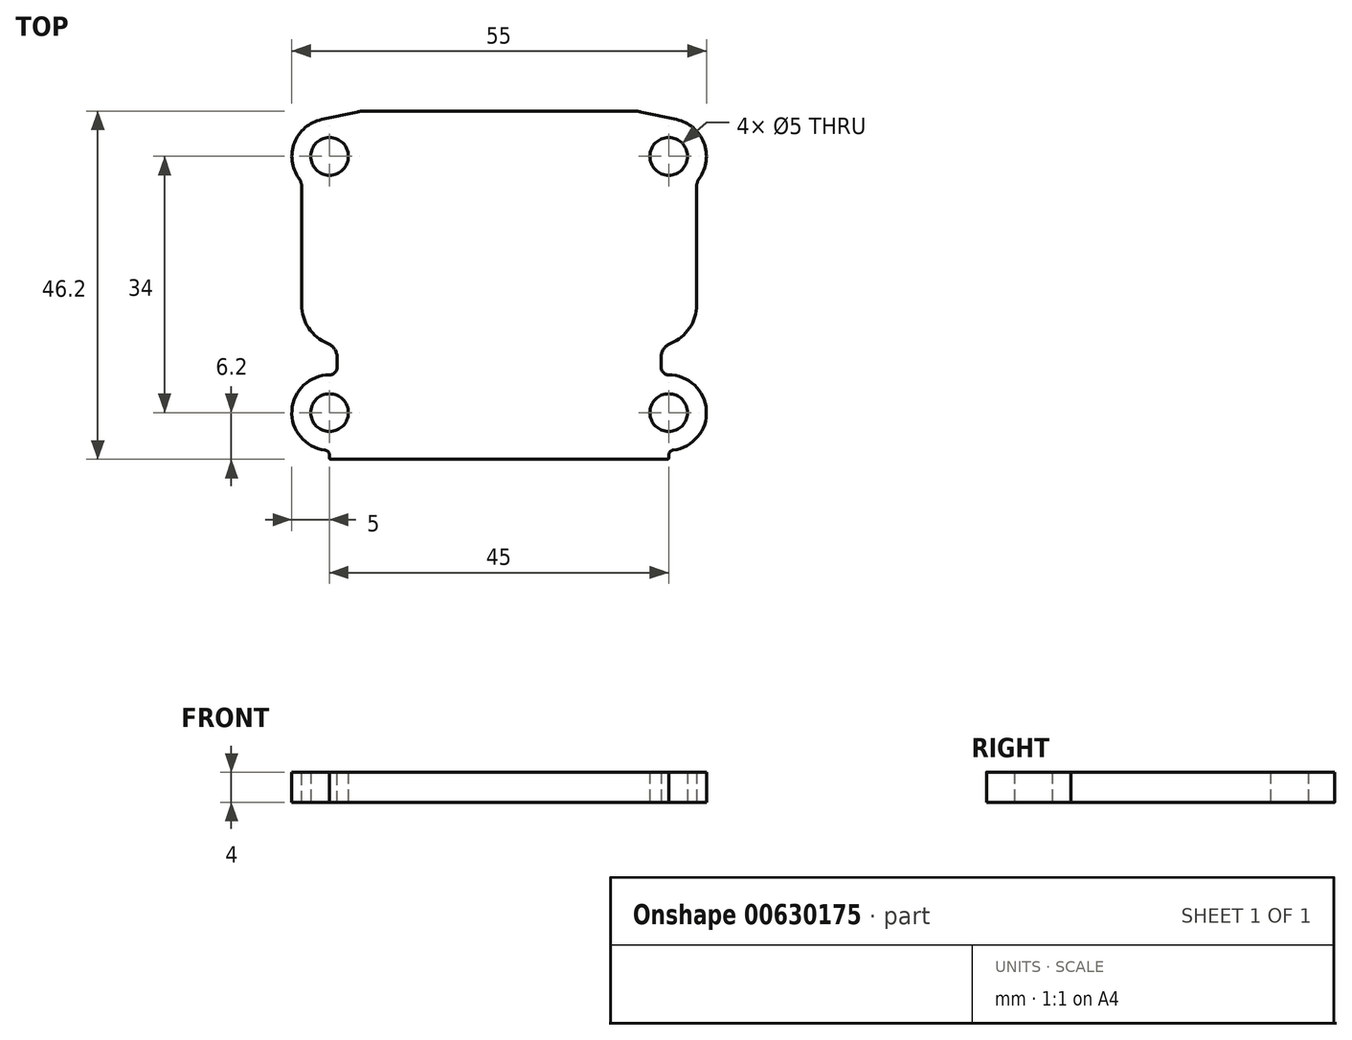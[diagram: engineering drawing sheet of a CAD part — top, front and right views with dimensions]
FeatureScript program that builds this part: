
annotation { "Feature Type Name" : "Feature", "Feature Type Description" : "" }
export const myFeature = defineFeature(function(context is Context, id is Id, definition is map)
    precondition{}
    {
        {
            var Q0;
            Q0=qCreatedBy(makeId("Top.planeOp"),FACE);
            var sketch = newSketch(context, id + "F0", { "sketchPlane" : qUnion([Q0])});
            skLineSegment(sketch, "E0.bottom", {"start": v(0, 0) * mm, "end": v(-45, 0) * mm, "construction": true});
            skLineSegment(sketch, "E0.top", {"start": v(0, 34) * mm, "end": v(-45, 34) * mm, "construction": true});
            skLineSegment(sketch, "E0.left", {"start": v(0, 0) * mm, "end": v(0, 34) * mm, "construction": true});
            skLineSegment(sketch, "E0.right", {"start": v(-45, 0) * mm, "end": v(-45, 34) * mm, "construction": true});
            skCircle(sketch, "E1", {"center": v(-45, 34) * mm, "radius": 2.5 * mm});
            skCircle(sketch, "E2", {"center": v(-45, 0) * mm, "radius": 2.5 * mm});
            skCircle(sketch, "E3", {"center": v(0, 0) * mm, "radius": 2.5 * mm});
            skArc(sketch, "E4", {"start": v(-44, 4.9) * mm, "mid": v(-49.97, 0.5) * mm, "end": v(-45, -5) * mm});
            skArc(sketch, "E5", {"start": v(0, -5) * mm, "mid": v(4.97, 0.5) * mm, "end": v(-1, 4.9) * mm});
            skLineSegment(sketch, "E6", {"start": v(-48.7, 30.64) * mm, "end": v(-48.7, 14.3) * mm});
            skLineSegment(sketch, "E7", {"start": v(-46.04, 38.9) * mm, "end": v(1.04, 38.9) * mm, "construction": true});
            skLineSegment(sketch, "E8", {"start": v(3.7, 30.64) * mm, "end": v(3.7, 14.3) * mm});
            skLineSegment(sketch, "E9", {"start": v(-40.82, 40) * mm, "end": v(-4.18, 40) * mm});
            skLineSegment(sketch, "E10", {"start": v(-4.18, 40) * mm, "end": v(1.04, 38.9) * mm});
            skLineSegment(sketch, "E11", {"start": v(-40.82, 40) * mm, "end": v(-46.04, 38.9) * mm});
            skLineSegment(sketch, "E12", {"start": v(-48.7, 14.3) * mm, "end": v(3.7, 14.3) * mm, "construction": true});
            skArc(sketch, "E13", {"start": v(-48.7, 14.3) * mm, "mid": v(-47.36, 10.7) * mm, "end": v(-44, 8.86) * mm});
            skArc(sketch, "E14", {"start": v(-1, 8.86) * mm, "mid": v(2.36, 10.7) * mm, "end": v(3.7, 14.3) * mm});
            skPoint(sketch, "E15", {"position": v(-45, 31.5) * mm});
            skPoint(sketch, "E16", {"position": v(-45, 2.5) * mm});
            skLineSegment(sketch, "E17.top", {"start": v(-45, -6.2) * mm, "end": v(0, -6.2) * mm});
            skLineSegment(sketch, "E17.left", {"start": v(-45, -5) * mm, "end": v(-45, -6.2) * mm});
            skLineSegment(sketch, "E17.right", {"start": v(0, -5) * mm, "end": v(0, -6.2) * mm});
            skLineSegment(sketch, "E18", {"start": v(-42.5, 0) * mm, "end": v(-42.5, 8.84) * mm, "construction": true});
            skLineSegment(sketch, "E19", {"start": v(-2.5, 0) * mm, "end": v(-2.5, 8.84) * mm, "construction": true});
            skLineSegment(sketch, "E20", {"start": v(-44, 8.86) * mm, "end": v(-44, 4.9) * mm});
            skLineSegment(sketch, "E21", {"start": v(-1, 8.86) * mm, "end": v(-1, 4.9) * mm});
            skCircle(sketch, "E22", {"center": v(0, 34) * mm, "radius": 2.5 * mm});
            skArc(sketch, "E23", {"start": v(-46.04, 38.9) * mm, "mid": v(-49.76, 35.53) * mm, "end": v(-48.7, 30.64) * mm});
            skArc(sketch, "E24", {"start": v(3.7, 30.64) * mm, "mid": v(4.76, 35.53) * mm, "end": v(1.04, 38.9) * mm});
            skSolve(sketch);
        }
        {
            var Q0;
            Q0 = qSketchRegion(id + "F0", true);
            extrude(context, id + "F1", {"entities" : qUnion([Q0]), "depth" : 4 * mm, "offsetDistance" : 25 * mm});
        }
        {
            var Q0;
            Q0=makeQuery(id+"F1.opExtrude","SWEPT_EDGE",EDGE,{"disambiguationData":[OSD([sQuery(id+"F0.wireOp",EDGE,"E13"),sQuery(id+"F0.wireOp",EDGE,"E20")])]});
            var Q1;
            Q1=makeQuery(id+"F1.opExtrude","SWEPT_EDGE",EDGE,{"disambiguationData":[OSD([sQuery(id+"F0.wireOp",EDGE,"E14"),sQuery(id+"F0.wireOp",EDGE,"E21")])]});
            fillet(context, id + "F2", {"entities" : qUnion([Q0, Q1]), "radius" : 2 * mm, "tangentPropagation" : true, "allowEdgeOverflow" : false});
        }
        {
            var Q0;
            Q0=makeQuery(id+"F1.opExtrude","SWEPT_EDGE",EDGE,{"disambiguationData":[OSD([sQuery(id+"F0.wireOp",EDGE,"E5"),sQuery(id+"F0.wireOp",EDGE,"E21")])]});
            var Q1;
            Q1=makeQuery(id+"F1.opExtrude","SWEPT_EDGE",EDGE,{"disambiguationData":[OSD([sQuery(id+"F0.wireOp",EDGE,"E4"),sQuery(id+"F0.wireOp",EDGE,"E20")])]});
            fillet(context, id + "F3", {"entities" : qUnion([Q0, Q1]), "radius" : 1 * mm, "tangentPropagation" : true, "allowEdgeOverflow" : false});
        }
        {
            var Q0;
            Q0=makeQuery(id+"F1.opExtrude","SWEPT_EDGE",EDGE,{"disambiguationData":[OSD([sQuery(id+"F0.wireOp",EDGE,"E4"),sQuery(id+"F0.wireOp",EDGE,"E17.left")])]});
            var Q1;
            Q1=makeQuery(id+"F1.opExtrude","SWEPT_EDGE",EDGE,{"disambiguationData":[OSD([sQuery(id+"F0.wireOp",EDGE,"E5"),sQuery(id+"F0.wireOp",EDGE,"E17.right")])]});
            fillet(context, id + "F4", {"entities" : qUnion([Q0, Q1]), "radius" : 0.7 * mm, "tangentPropagation" : true, "defaultsChanged" : true, "vertexSettings" : [], "allowEdgeOverflow" : false});
        }
        {
            var Q0;
            Q0=makeQuery(id+"F1.opExtrude","SWEPT_EDGE",EDGE,{"disambiguationData":[OSD([sQuery(id+"F0.wireOp",EDGE,"E17.top"),sQuery(id+"F0.wireOp",EDGE,"E17.left")])]});
            var Q1;
            Q1=makeQuery(id+"F1.opExtrude","SWEPT_EDGE",EDGE,{"disambiguationData":[OSD([sQuery(id+"F0.wireOp",EDGE,"E17.top"),sQuery(id+"F0.wireOp",EDGE,"E17.right")])]});
            fillet(context, id + "F5", {"entities" : qUnion([Q0, Q1]), "radius" : 0.2 * mm, "tangentPropagation" : true, "allowEdgeOverflow" : false});
        }
        {
            var Q0;
            Q0=makeQuery(id+"F1.opExtrude","SWEPT_EDGE",EDGE,{"disambiguationData":[OSD([sQuery(id+"F0.wireOp",EDGE,"E6"),sQuery(id+"F0.wireOp",EDGE,"E23")])]});
            var Q1;
            Q1=makeQuery(id+"F1.opExtrude","SWEPT_EDGE",EDGE,{"disambiguationData":[OSD([sQuery(id+"F0.wireOp",EDGE,"E8"),sQuery(id+"F0.wireOp",EDGE,"zDeX1Jgn-uE8p-g2Hl-jD29-gbyf43CDi7m2")])]});
            fillet(context, id + "F6", {"entities" : qUnion([Q0, Q1]), "radius" : 2 * mm, "tangentPropagation" : true, "defaultsChanged" : false, "vertexSettings" : [], "allowEdgeOverflow" : false});
        }
        {
            var Q0;
            Q0=makeQuery(id+"F1.opExtrude","SWEPT_EDGE",EDGE,{"disambiguationData":[OSD([sQuery(id+"F0.wireOp",EDGE,"E9"),sQuery(id+"F0.wireOp",EDGE,"E11")])]});
            var Q1;
            Q1=makeQuery(id+"F1.opExtrude","SWEPT_EDGE",EDGE,{"disambiguationData":[OSD([sQuery(id+"F0.wireOp",EDGE,"E9"),sQuery(id+"F0.wireOp",EDGE,"E10")])]});
            fillet(context, id + "F7", {"entities" : qUnion([Q0, Q1]), "radius" : 5 * mm, "tangentPropagation" : true, "allowEdgeOverflow" : false});
        }
    });
